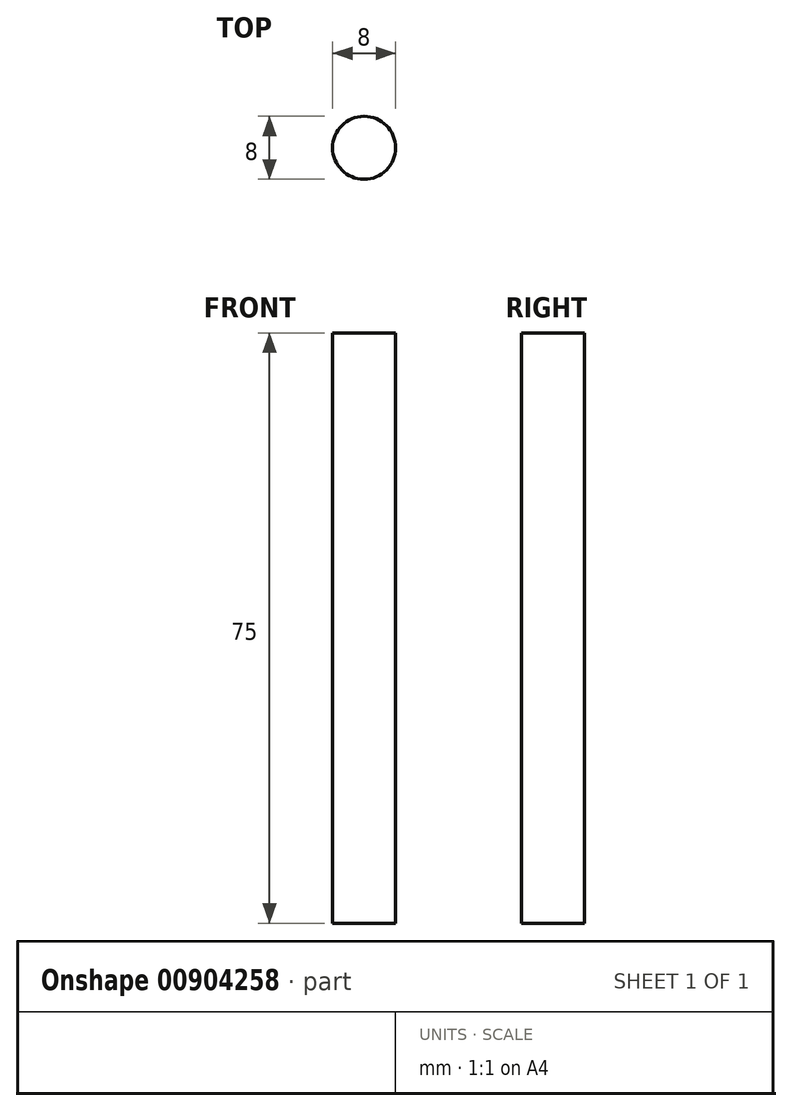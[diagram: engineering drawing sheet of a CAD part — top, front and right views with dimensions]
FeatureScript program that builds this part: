
annotation { "Feature Type Name" : "Feature", "Feature Type Description" : "" }
export const myFeature = defineFeature(function(context is Context, id is Id, definition is map)
    precondition{}
    {
        {
            var Q0;
            Q0=qCreatedBy(makeId("Front.planeOp"),FACE);
            var sketch = newSketch(context, id + "F0", { "sketchPlane" : qUnion([Q0])});
            skLineSegment(sketch, "E0.bottom", {"start": v(0, 0) * mm, "end": v(-4, 0) * mm});
            skLineSegment(sketch, "E0.top", {"start": v(0, 75) * mm, "end": v(-4, 75) * mm});
            skLineSegment(sketch, "E0.left", {"start": v(0, 0) * mm, "end": v(0, 75) * mm});
            skLineSegment(sketch, "E0.right", {"start": v(-4, 0) * mm, "end": v(-4, 75) * mm});
            skSolve(sketch);
        }
        {
            var Q0;
            Q0=makeQuery(id+"F0.imprint","IMPRINT",FACE,{"disambiguationData":[TD([[makeQuery(id+"F0.imprint","IMPRINT",EDGE,{"derivedFrom":sQuery(id+"F0.wireOp",EDGE,"E0.bottom")}),-1.0]])]});
            var Q1;
            Q1=sQuery(id+"F0.wireOp",EDGE,"E0.left");
            revolve(context, id + "F1", {"surfaceOperationType" : NewSurfaceOperationType.NEW, "entities" : qUnion([Q0]), "axis" : qUnion([Q1]), "revolveType" : RevolveType.FULL});
        }
    });
